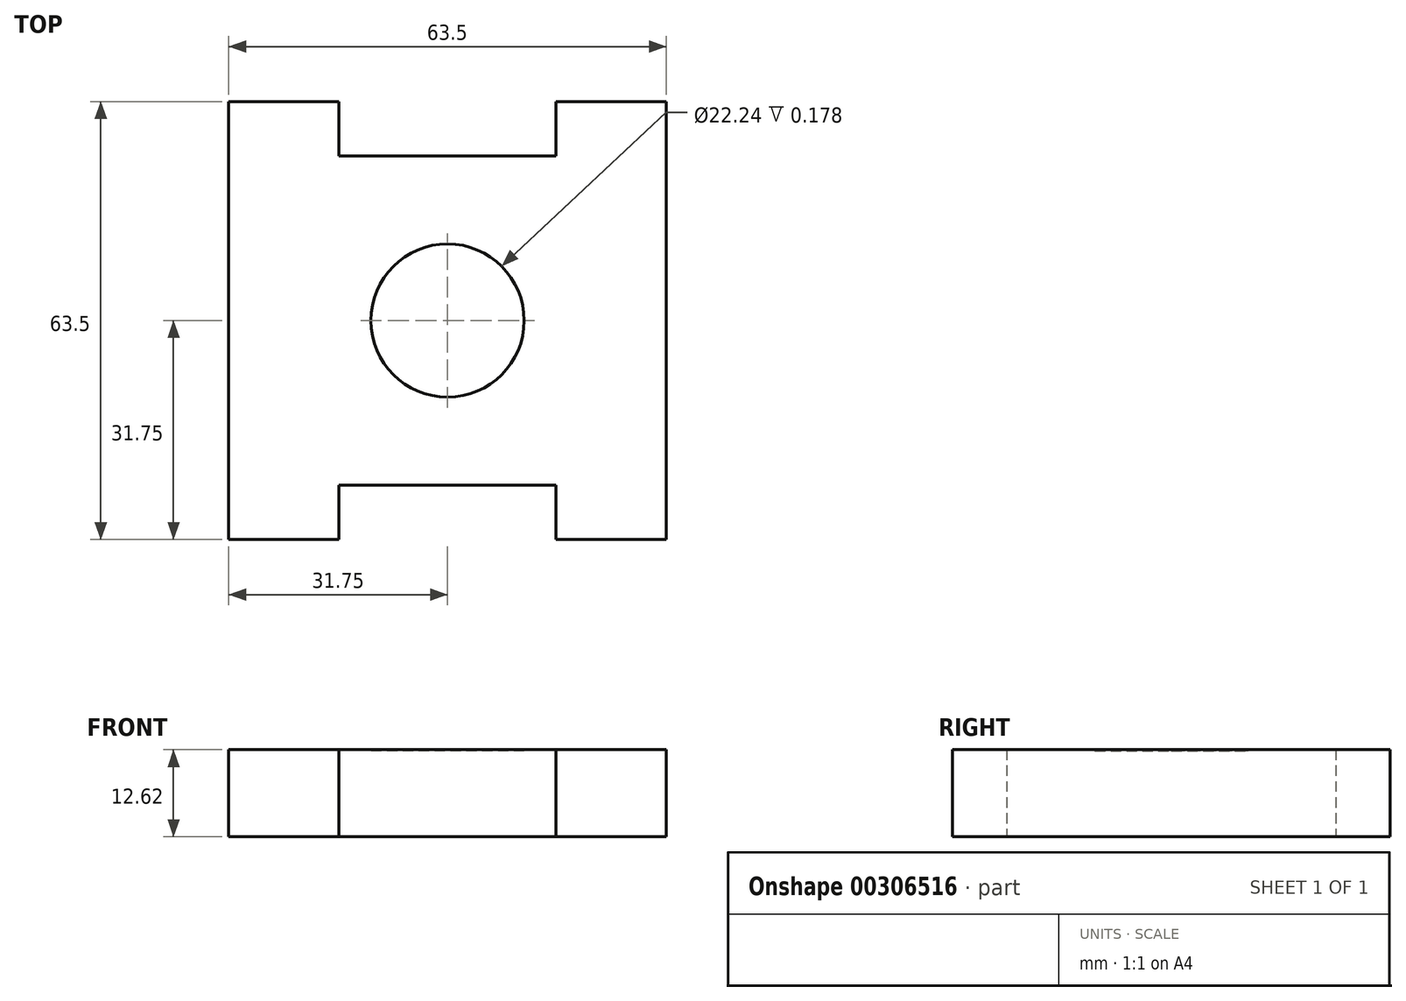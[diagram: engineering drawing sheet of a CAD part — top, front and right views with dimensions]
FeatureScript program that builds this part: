
annotation { "Feature Type Name" : "Feature", "Feature Type Description" : "" }
export const myFeature = defineFeature(function(context is Context, id is Id, definition is map)
    precondition{}
    {
        {
            var Q0;
            Q0=qCreatedBy(makeId("Top.planeOp"),FACE);
            var sketch = newSketch(context, id + "F0", { "sketchPlane" : qUnion([Q0])});
            skLineSegment(sketch, "E0", {"start": v(-63.5, 63.5) * mm, "end": v(-63.5, 0) * mm});
            skLineSegment(sketch, "E1", {"start": v(-63.5, 0) * mm, "end": v(-47.5, 0) * mm});
            skLineSegment(sketch, "E2", {"start": v(-47.5, 0) * mm, "end": v(-47.5, 7.87) * mm});
            skLineSegment(sketch, "E3", {"start": v(-47.5, 7.87) * mm, "end": v(-16, 7.87) * mm});
            skLineSegment(sketch, "E4", {"start": v(-16, 7.87) * mm, "end": v(-16, 0) * mm});
            skLineSegment(sketch, "E5", {"start": v(-16, 0) * mm, "end": v(0, 0) * mm});
            skLineSegment(sketch, "E6", {"start": v(0, 0) * mm, "end": v(0, 63.5) * mm});
            skLineSegment(sketch, "E7", {"start": v(0, 63.5) * mm, "end": v(-16, 63.5) * mm});
            skLineSegment(sketch, "E8", {"start": v(-16, 63.5) * mm, "end": v(-16, 55.63) * mm});
            skLineSegment(sketch, "E9", {"start": v(-16, 55.63) * mm, "end": v(-47.5, 55.63) * mm});
            skLineSegment(sketch, "E10", {"start": v(-47.5, 55.63) * mm, "end": v(-47.5, 63.5) * mm});
            skLineSegment(sketch, "E11", {"start": v(-47.5, 63.5) * mm, "end": v(-63.5, 63.5) * mm});
            skCircle(sketch, "E12", {"center": v(-31.75, 31.75) * mm, "radius": 11.12 * mm});
            skSolve(sketch);
        }
        {
            var Q0;
            Q0 = qSketchRegion(id + "F0", true);
            extrude(context, id + "F1", {"entities" : qUnion([Q0]), "depth" : 25.4 * mm});
        }
        {
            var Q0;
            Q0=makeQuery(id+"F1.opExtrude","CAP_FACE",FACE,{"disambiguationData":[OSD([sQuery(id+"F0.wireOp",EDGE,"E0"),sQuery(id+"F0.wireOp",EDGE,"E1"),sQuery(id+"F0.wireOp",EDGE,"E2"),sQuery(id+"F0.wireOp",EDGE,"E3"),sQuery(id+"F0.wireOp",EDGE,"E4"),sQuery(id+"F0.wireOp",EDGE,"E5"),sQuery(id+"F0.wireOp",EDGE,"E6"),sQuery(id+"F0.wireOp",EDGE,"E7"),sQuery(id+"F0.wireOp",EDGE,"E8"),sQuery(id+"F0.wireOp",EDGE,"E9"),sQuery(id+"F0.wireOp",EDGE,"E10"),sQuery(id+"F0.wireOp",EDGE,"E11"),sQuery(id+"F0.wireOp",EDGE,"E12")])],"isStart":false});
            extrude(context, id + "F2", {"entities" : qUnion([Q0]), "operationType" : NewBodyOperationType.ADD, "depth" : 12.7 * mm});
        }
        {
            var Q0;
            Q0=makeQuery(id+"F2.opExtrude","CAP_FACE",FACE,{"disambiguationData":[OSD([sQuery(id+"F0.wireOp",EDGE,"E0"),sQuery(id+"F0.wireOp",EDGE,"E1"),sQuery(id+"F0.wireOp",EDGE,"E2"),sQuery(id+"F0.wireOp",EDGE,"E3"),sQuery(id+"F0.wireOp",EDGE,"E4"),sQuery(id+"F0.wireOp",EDGE,"E5"),sQuery(id+"F0.wireOp",EDGE,"E6"),sQuery(id+"F0.wireOp",EDGE,"E7"),sQuery(id+"F0.wireOp",EDGE,"E8"),sQuery(id+"F0.wireOp",EDGE,"E9"),sQuery(id+"F0.wireOp",EDGE,"E10"),sQuery(id+"F0.wireOp",EDGE,"E11"),sQuery(id+"F0.wireOp",EDGE,"E12")])],"isStart":false});
            extrude(context, id + "F3", {"entities" : qUnion([Q0]), "operationType" : NewBodyOperationType.REMOVE, "oppositeDirection" : true, "depth" : 12.7 * mm});
        }
        {
            var Q0;
            Q0=makeQuery(id+"F3.boolean.opBoolean","COPY",FACE,{"derivedFrom":makeQuery(id+"F3.opExtrude","CAP_FACE",FACE,{"disambiguationData":[OSD([sQuery(id+"F0.wireOp",EDGE,"E0"),sQuery(id+"F0.wireOp",EDGE,"E1"),sQuery(id+"F0.wireOp",EDGE,"E2"),sQuery(id+"F0.wireOp",EDGE,"E3"),sQuery(id+"F0.wireOp",EDGE,"E4"),sQuery(id+"F0.wireOp",EDGE,"E5"),sQuery(id+"F0.wireOp",EDGE,"E6"),sQuery(id+"F0.wireOp",EDGE,"E7"),sQuery(id+"F0.wireOp",EDGE,"E8"),sQuery(id+"F0.wireOp",EDGE,"E9"),sQuery(id+"F0.wireOp",EDGE,"E10"),sQuery(id+"F0.wireOp",EDGE,"E11"),sQuery(id+"F0.wireOp",EDGE,"E12")])],"isStart":false})});
            extrude(context, id + "F4", {"entities" : qUnion([Q0]), "operationType" : NewBodyOperationType.REMOVE, "oppositeDirection" : true, "depth" : 12.78 * mm});
        }
        {
            var Q0;
            Q0=makeQuery(id+"F0.imprint","IMPRINT",FACE,{"disambiguationData":[TD([[makeQuery(id+"F0.imprint","IMPRINT",EDGE,{"derivedFrom":sQuery(id+"F0.wireOp",EDGE,"E12")}),1.0]])]});
            extrude(context, id + "F5", {"entities" : qUnion([Q0]), "operationType" : NewBodyOperationType.ADD, "depth" : 0.5 * mm});
        }
        {
            var Q0;
            Q0=makeQuery(id+"F5.opExtrude","CAP_FACE",FACE,{"disambiguationData":[OSD([sQuery(id+"F0.wireOp",EDGE,"E12")])],"isStart":false});
            extrude(context, id + "F6", {"entities" : qUnion([Q0]), "operationType" : NewBodyOperationType.ADD, "depth" : 11.94 * mm});
        }
    });
